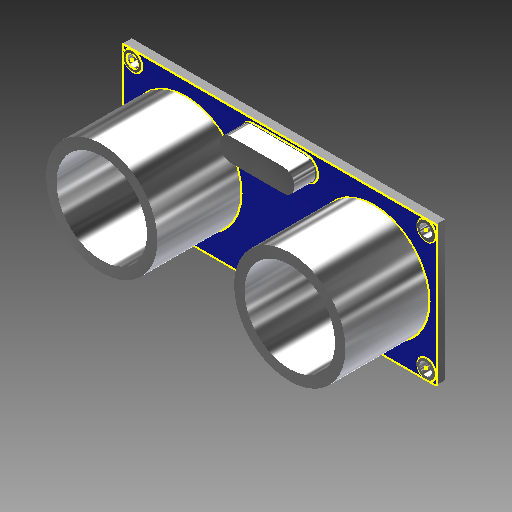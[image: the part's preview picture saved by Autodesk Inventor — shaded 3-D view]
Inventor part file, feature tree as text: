
AUTODESK INVENTOR PART (.ipt)
format: ipt  version: 2017 (Build 210142000, 142)  size: 477,696 bytes
history: native  units: mm
features: sketch x23, projected_geometry x17, extrude x15, revolve x4
ambient origin geometry x8: Origin, YZ Plane, XZ Plane, XY Plane, X Axis, Y Axis, Z Axis, Center Point
bodies: Solid1 (feature_tree)
feature tree (59):
  extrude  "Extrusion1"  Depth=20.0mm
  extrude  "Extrusion2"  Depth=7.0mm TaperAngle=0.0deg
  extrude  "Extrusion3"  Depth=7.0mm TaperAngle=0.0deg
  extrude  "Extrusion4"  Depth=13.0mm
  extrude  "Extrusion5"  Depth=5.0mm TaperAngle=0.0deg
  extrude  "Extrusion6"  Depth=0.2mm TaperAngle=0.0deg
  extrude  "Extrusion7"  Depth=3.0mm
  extrude  "Extrusion8"  Depth=2.0mm
  extrude  "Extrusion9"  Depth=0.1mm TaperAngle=0.0deg
  extrude  "Extrusion10"  Depth=0.1mm TaperAngle=0.0deg
  extrude  "Extrusion11"  TaperAngle=90.0deg  [1 undecoded]
  revolve  "Revolution1"  Angle=180.0deg
  revolve  "Revolution2"  [1 undecoded]
  revolve  "Revolution3"  [1 undecoded]
  revolve  "Revolution4"  [1 undecoded]
  extrude  "Extrusion12"  Depth=8.0mm TaperAngle=0.0deg
  sketch  "Sketch17"  dims[d68=0.5mm d69=0.5mm]
  sketch  "Sketch18"  dims[d70=80.0mm d71=0.0mm]
  extrude  "Extrusion13"  Depth=0.5mm
  extrude  "Extrusion14"  [1 undecoded]
  extrude  "Extrusion15"  [1 undecoded]
  sketch  "Sketch22"
  sketch  "Sketch23"
  sketch  "Sketch1"  dims[d0=45.0mm d1=20.0mm]
  sketch  "Sketch2"  dims[d2=1.3mm d3=0.0mm d6=7.0mm d7=0.0mm]
  sketch  "Sketch3"  dims[d13=7.0mm d14=0.0mm d19=7.0mm d20=0.0mm]
  sketch  "Sketch4"  dims[d21=13.0mm d22=13.0mm]
  sketch  "Sketch5"  dims[d23=10.0mm d24=0.0mm d25=5.0mm d26=0.0mm]
  projected_geometry  "Projected Loop1"
  projected_geometry  "Projected Loop2"
  sketch  "Sketch6"  dims[d27=1.0mm d28=0.0mm d36=0.2mm d37=0.0mm]
  projected_geometry  "Projected Loop3"
  projected_geometry  "Projected Loop4"
  sketch  "Sketch7"  dims[d42=3.0mm d43=0.0mm d44=2.7mm]
  projected_geometry  "Projected Loop5"
  sketch  "Sketch8"  dims[d45=2.7mm d46=2.0mm]
  projected_geometry  "Projected Loop6"
  sketch  "Sketch9"  dims[d47=2.7mm d48=0.1mm d49=0.0mm]
  projected_geometry  "Projected Loop7"
  sketch  "Sketch10"  dims[d50=2.7mm d51=0.1mm d52=0.0mm]
  projected_geometry  "Projected Loop8"
  sketch  "Sketch11"  dims[d53=90.0deg d54=90.0deg]
  sketch  "Sketch12"  dims[d55=180.0deg d56=180.0deg]
  projected_geometry  "Projected Loop9"
  sketch  "Sketch13"  dims[d57=180.0deg d58=2.0mm]
  projected_geometry  "Projected Loop10"
  sketch  "Sketch14"  dims[d59=2.0mm d60=2.0mm]
  sketch  "Sketch15"  dims[d61=2.0mm d62=2.0mm d63=0.0mm]
  sketch  "Sketch16"  dims[d64=2.0mm d65=0.0mm d66=8.0mm d67=0.0mm]
  projected_geometry  "Projected Loop11"
  sketch  "Sketch19"
  projected_geometry  "Projected Loop12"
  sketch  "Sketch20"
  projected_geometry  "Projected Loop13"
  projected_geometry  "Projected Loop14"
  projected_geometry  "Projected Loop15"
  sketch  "Sketch21"
  projected_geometry  "Projected Loop16"
  projected_geometry  "Projected Loop17"
note: 6 required parameter values undecoded (feature->parameter linkage not recoverable at this tier; creation-order binding heuristic only, values carry confidence <= 0.55)